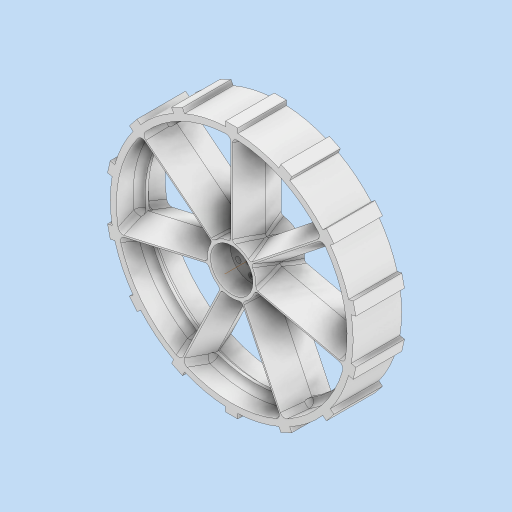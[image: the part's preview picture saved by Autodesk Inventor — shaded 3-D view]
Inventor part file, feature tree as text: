
AUTODESK INVENTOR PART (.ipt)
format: ipt  version: 2023 (Build 270158000, 158)  size: 1,228,800 bytes
history: native  units: in
note: dims shown in document units (in); Inventor stores cm internally (conversion verified against a paired STEP export)
features: extrude x6, sketch x6, pattern_circular x5, projected_geometry x5, fillet x3, mirror x2, plane x1
ambient origin geometry x8: Origin, YZ Plane, XZ Plane, XY Plane, X Axis, Y Axis, Z Axis, Center Point
bodies: Solid1 (feature_tree)
feature tree (28):
  extrude  "Extrusion1"  Depth=0.25in
  extrude  "Extrusion2"  TaperAngle=0.0deg  [1 undecoded]
  extrude  "Extrusion3"  Depth=0.5787in
  extrude  "Extrusion4"  Depth=0.625in
  pattern_circular  "Circular Pattern1"  Count=6 Angle=360.0deg
  extrude  "Extrusion5"  TaperAngle=0.0deg  [1 undecoded]
  plane  "Work Plane1"
  extrude  "Extrusion6"  Depth=0.0787in
  pattern_circular  "Circular Pattern2"  [2 undecoded]
  fillet  "Fillet1"  [1 undecoded]
  mirror  "Mirror1"
  pattern_circular  "Circular Pattern3"  Count=2  [1 undecoded]
  fillet  "Fillet2"  Radius=0.0787in
  mirror  "Mirror2"
  pattern_circular  "Circular Pattern4"  [2 undecoded]
  fillet  "Fillet4"  Radius=0.0787in
  pattern_circular  "Circular Pattern6"  [2 undecoded]
  sketch  "Sketch1"  dims[d0=10.0in d2=0.25in]
  sketch  "Sketch2"  dims[d3=2.0in d4=0.0in]
  sketch  "Sketch3"  dims[d5=2.0in d7=0.5787in]
  sketch  "Sketch4"  dims[d8=0.2362in d9=0.625in d10=2.3622in d12=360.0deg]
  sketch  "Sketch5"  dims[d14=0.375in d15=0.0in]
  sketch  "Sketch6"  dims[d16=2.0in d17=0.125in d18=2.0in d19=0.0in d21=0.7874in d22=0.0787in d23=0.0787in d24=0.0787in d25=0.063in d26=2.0in d27=0.0in d28=2.7559in d29=360.0deg d32=0.125in d33=0.0in d34=2.0in d35=0.5in d36=4.9375in d37=0.25in d38=0.0in d39=5.5118in d40=360.0deg d42=0.25in d43=2.7559in d44=360.0deg d46=0.1969in d47=2.7559in d48=360.0deg d54=0.1181in d55=2.7559in d56=360.0deg]
  projected_geometry  "Project Cut Edges1"
  projected_geometry  "Project Cut Edges2"
  projected_geometry  "Project Cut Edges3"
  projected_geometry  "Project Cut Edges4"
  projected_geometry  "Project Cut Edges5"
note: 10 required parameter values undecoded (feature->parameter linkage not recoverable at this tier; creation-order binding heuristic only, values carry confidence <= 0.55)
